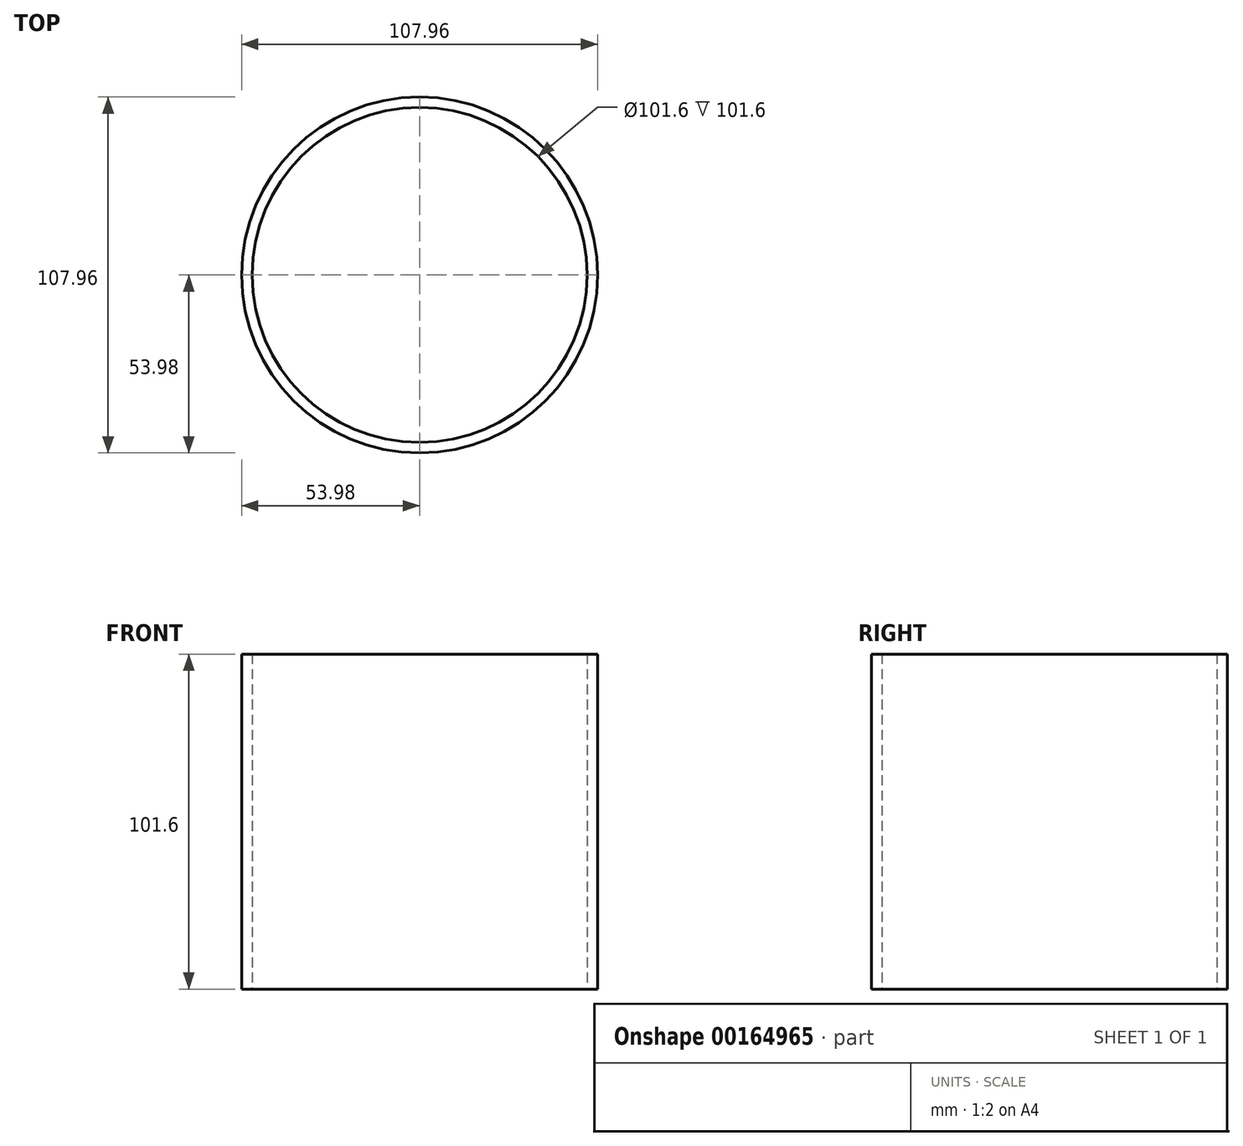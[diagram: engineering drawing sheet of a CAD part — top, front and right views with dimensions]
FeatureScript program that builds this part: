
annotation { "Feature Type Name" : "Feature", "Feature Type Description" : "" }
export const myFeature = defineFeature(function(context is Context, id is Id, definition is map)
    precondition{}
    {
        {
            var Q0;
            Q0=qCreatedBy(makeId("Top.planeOp"),FACE);
            var sketch = newSketch(context, id + "F0", { "sketchPlane" : qUnion([Q0])});
            skCircle(sketch, "E0", {"center": v(0, 0) * mm, "radius": 50.8 * mm});
            skCircle(sketch, "E1", {"center": v(0, 0) * mm, "radius": 53.97 * mm});
            skSolve(sketch);
        }
        {
            var Q0;
            Q0 = qSketchRegion(id + "F0", true);
            extrude(context, id + "F1", {"entities" : qUnion([Q0]), "depth" : 101.6 * mm});
        }
    });
